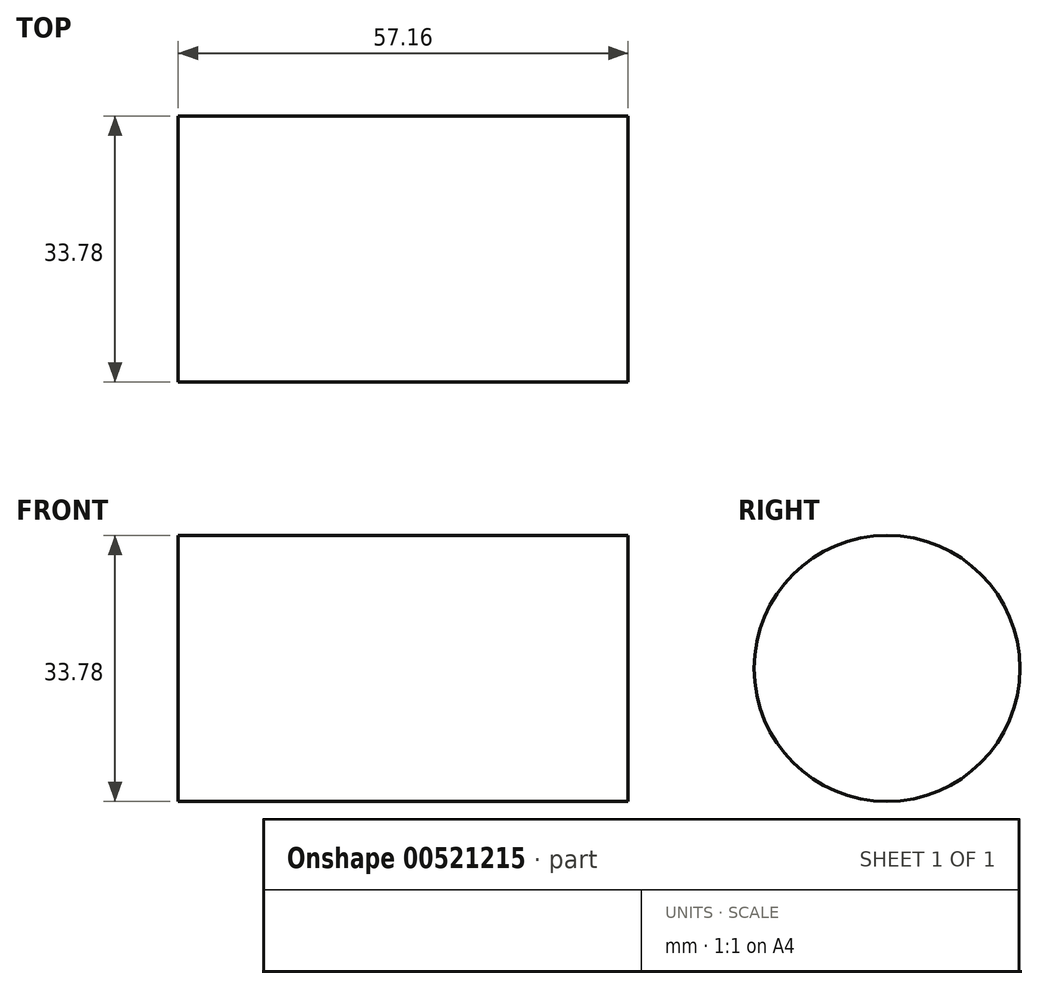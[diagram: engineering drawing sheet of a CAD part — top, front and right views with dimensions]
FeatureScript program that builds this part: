
annotation { "Feature Type Name" : "Feature", "Feature Type Description" : "" }
export const myFeature = defineFeature(function(context is Context, id is Id, definition is map)
    precondition{}
    {
        {
            var Q0;
            Q0=qCreatedBy(makeId("Right.planeOp"),FACE);
            var sketch = newSketch(context, id + "F0", { "sketchPlane" : qUnion([Q0])});
            skCircle(sketch, "E0.0", {"center": v(0, 0) * mm, "radius": 16.9 * mm});
            skSolve(sketch);
        }
        {
            var Q0;
            Q0 = qSketchRegion(id + "F0", true);
            extrude(context, id + "F1", {"entities" : qUnion([Q0]), "depth" : 28.57 * mm, "offsetDistance" : 25.4 * mm, "hasSecondDirection" : true, "secondDirectionOppositeDirection" : true, "secondDirectionDepth" : 28.57 * mm});
        }
    });
